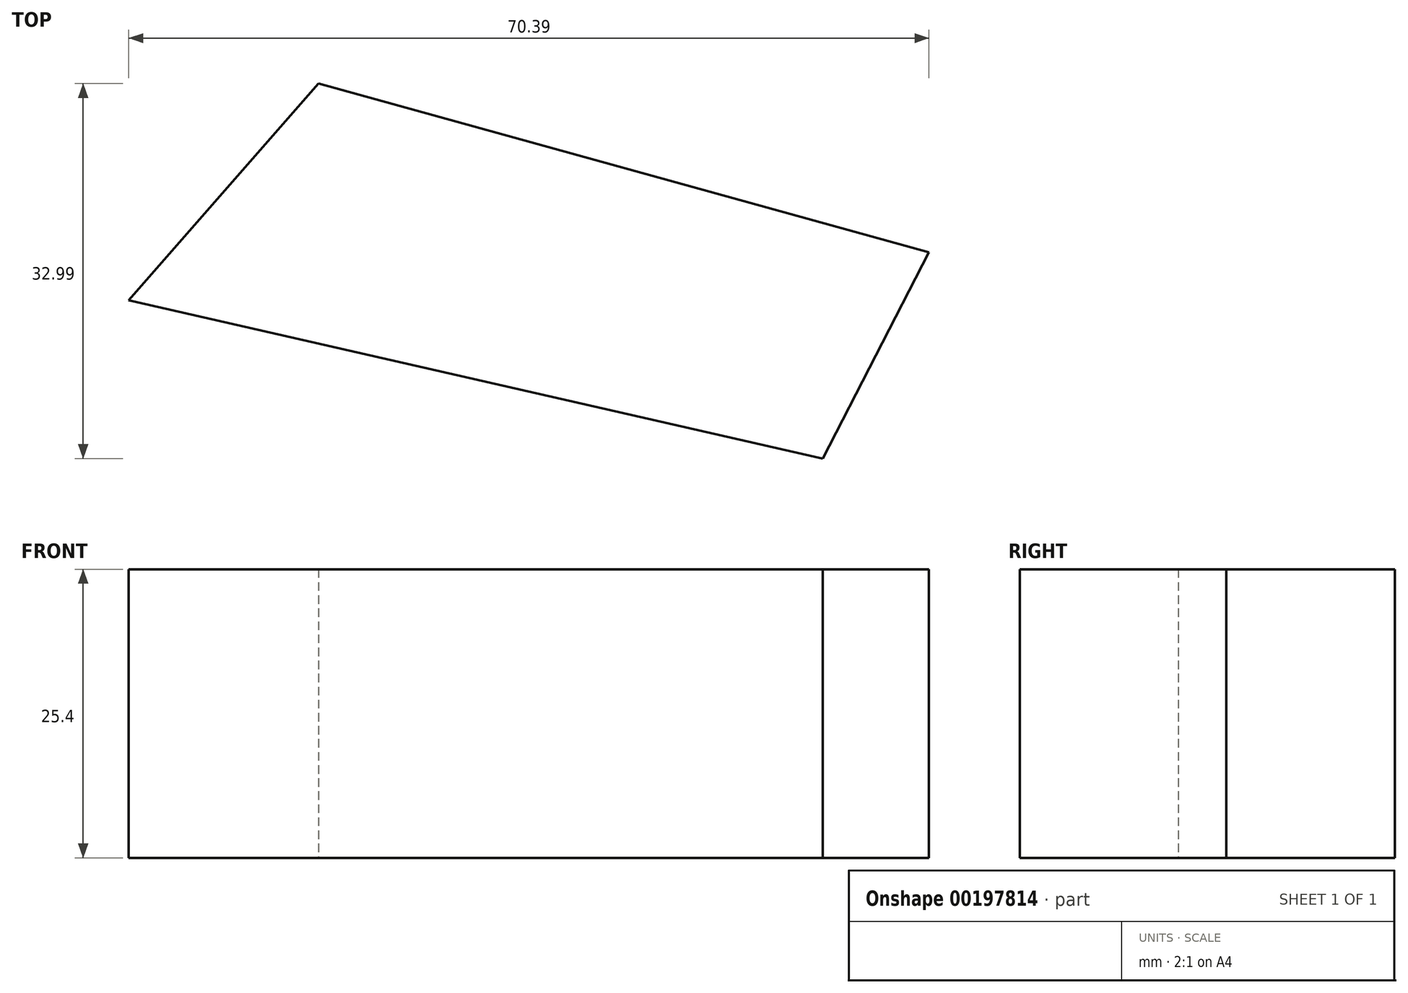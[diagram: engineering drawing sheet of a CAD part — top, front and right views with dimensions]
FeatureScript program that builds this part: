
annotation { "Feature Type Name" : "Feature", "Feature Type Description" : "" }
export const myFeature = defineFeature(function(context is Context, id is Id, definition is map)
    precondition{}
    {
        {
            var Q0;
            Q0=qCreatedBy(makeId("Top.planeOp"),FACE);
            var sketch = newSketch(context, id + "F0", { "sketchPlane" : qUnion([Q0])});
            skLineSegment(sketch, "E0", {"start": v(-19.98, 40.78) * mm, "end": v(-36.66, 21.72) * mm});
            skLineSegment(sketch, "E1", {"start": v(-36.66, 21.72) * mm, "end": v(24.38, 7.8) * mm});
            skLineSegment(sketch, "E2", {"start": v(-19.98, 40.78) * mm, "end": v(33.73, 25.94) * mm});
            skLineSegment(sketch, "E3", {"start": v(33.73, 25.94) * mm, "end": v(24.38, 7.8) * mm});
            skSolve(sketch);
        }
        {
            var Q0;
            Q0=makeQuery(id+"F0.imprint","IMPRINT",FACE,{"disambiguationData":[TD([[makeQuery(id+"F0.imprint","IMPRINT",EDGE,{"derivedFrom":sQuery(id+"F0.wireOp",EDGE,"E0")}),1.0]])]});
            extrude(context, id + "F1", {"entities" : qUnion([Q0]), "depth" : 25.4 * mm});
        }
    });
